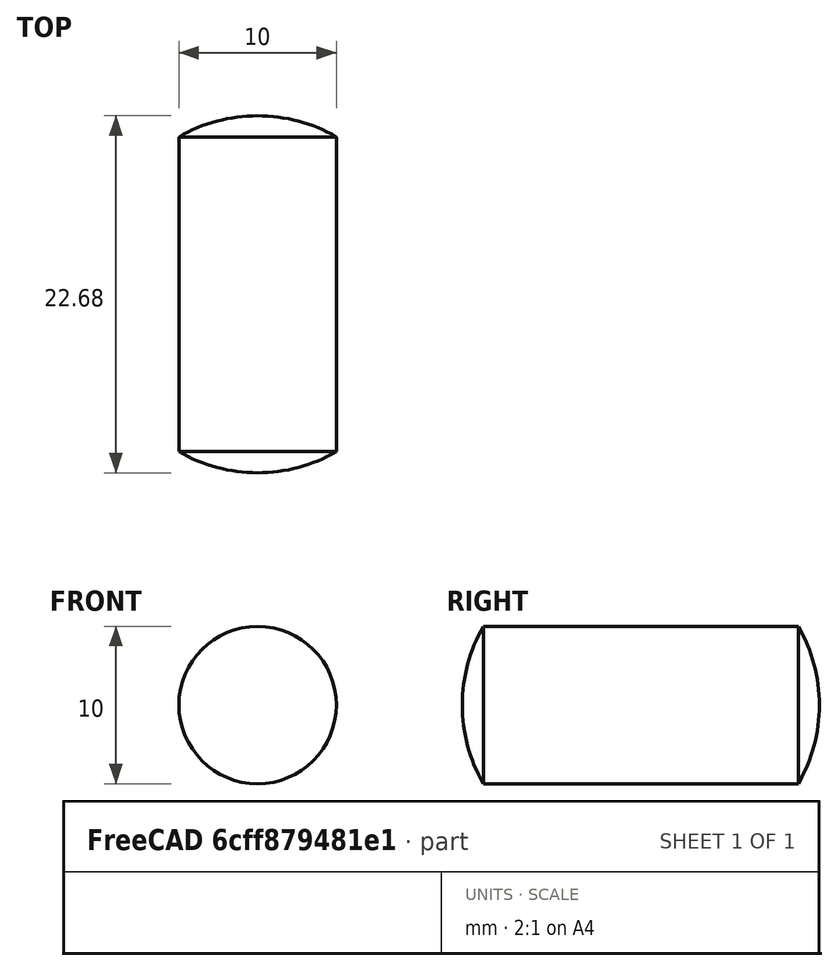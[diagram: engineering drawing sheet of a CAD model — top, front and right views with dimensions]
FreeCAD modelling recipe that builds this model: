
FCSTD DOCUMENT  (FreeCAD 0.15R4470 (Git))
Label: Zyl-Stift_DIN_7-10x10
License: CC-BY 3.0
LicenseURL: http://creativecommons.org/licenses/by/3.0/
objects: Sketcher::SketchObject×1, PartDesign::Revolution×1
note: 3 computed .brp shape members not serialized (recipe doc carries the construction recipe); baked Part::Feature solids carry a one-line shape summary decoded from their .brp

FEATURE [Sketcher::SketchObject] Sketch
  Placement = pos=(0,0,0) rot=(0.57735,0.57735,0.57735;2.0944rad)
  sketch-geometry (4):
    g0: ArcOfCircle CenterX=11.3397 CenterY=0 CenterZ=0 NormalX=0 NormalY=0 NormalZ=1 Radius=10 StartAngle=0 EndAngle=0.523599
    g1: LineSegment StartX=-1.2e-11 StartY=5 StartZ=0 EndX=20 EndY=5 EndZ=0
    g2: LineSegment StartX=-1.33975 StartY=0 StartZ=0 EndX=21.3397 EndY=0 EndZ=0
    g3: ArcOfCircle CenterX=8.66025 CenterY=0 CenterZ=0 NormalX=0 NormalY=0 NormalZ=1 Radius=10 StartAngle=2.61799 EndAngle=3.14159
  constraints (14):
    c: PointOnObject(g2,g-1)
    c: PointOnObject(g1,g-2)
    c: Coincident(g0,g1)
    c: PointOnObject(g0,g-1)
    c: Horizontal(g1)
    c: Coincident(g2,g0)
    c: Horizontal(g2)
    c: Radius(g0) = 10
    c: PointOnObject(g3,g2)
    c: Coincident(g3,g1)
    c: Coincident(g3,g2)
    c: Equal(g3,g0)
    c: DistanceY(g-1,g1) = 5
    c: DistanceX(g1) = 20
FEATURE [PartDesign::Revolution] Revolution  label="Zyl-Stift DIN 7-10x20 #"
  Angle = 360
  Axis = (0,1,0)
  Base = (0,0,0)
  Placement = pos=(0,0,0) rot=(0.57735,0.57735,0.57735;2.0944rad)
  ReferenceAxis = -> Sketch [H_Axis]
  Sketch = -> Sketch
